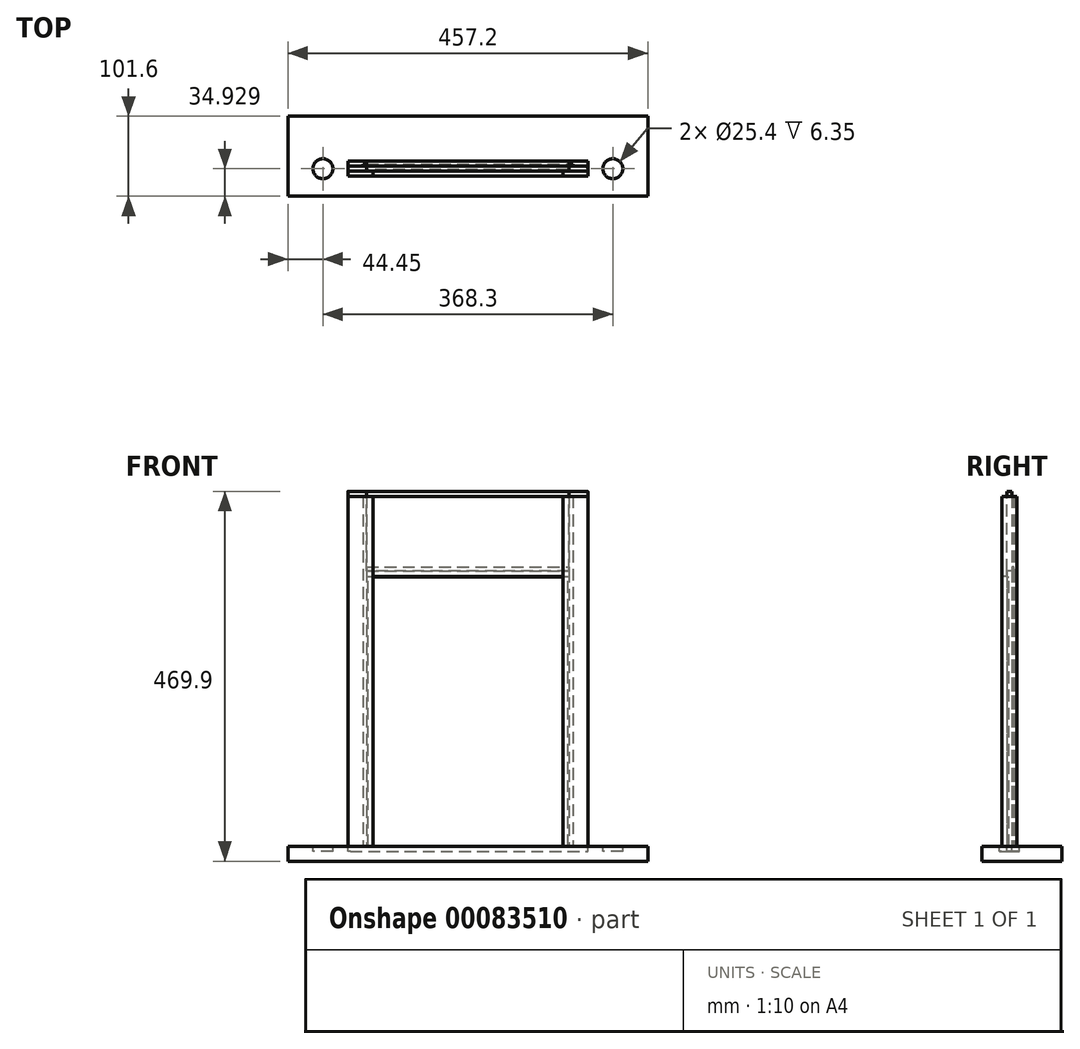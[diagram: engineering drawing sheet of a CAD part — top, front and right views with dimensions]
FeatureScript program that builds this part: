
annotation { "Feature Type Name" : "Feature", "Feature Type Description" : "" }
export const myFeature = defineFeature(function(context is Context, id is Id, definition is map)
    precondition{}
    {
        {
            var Q0;
            Q0=qCreatedBy(makeId("Front.planeOp"),FACE);
            var sketch = newSketch(context, id + "F0", { "sketchPlane" : qUnion([Q0])});
            skLineSegment(sketch, "E0.bottom", {"start": v(-127, -6.35) * mm, "end": v(127, -6.35) * mm});
            skLineSegment(sketch, "E0.top", {"start": v(-127, 349.25) * mm, "end": v(127, 349.25) * mm});
            skLineSegment(sketch, "E0.left", {"start": v(-127, -6.35) * mm, "end": v(-127, 349.25) * mm});
            skLineSegment(sketch, "E0.right", {"start": v(127, -6.35) * mm, "end": v(127, 349.25) * mm});
            skPoint(sketch, "E1", {"position": v(0, -6.35) * mm});
            skSolve(sketch);
        }
        {
            var Q0;
            Q0 = qSketchRegion(id + "F0", true);
            extrude(context, id + "F1", {"entities" : qUnion([Q0]), "depth" : 0.25 * mm});
        }
        {
            var Q0;
            Q0=qCreatedBy(makeId("Top.planeOp"),FACE);
            var sketch = newSketch(context, id + "F2", { "sketchPlane" : qUnion([Q0])});
            skLineSegment(sketch, "E2", {"start": v(-128.59, -2.29) * mm, "end": v(-120.65, -2.29) * mm});
            skLineSegment(sketch, "E3", {"start": v(-120.65, -2.29) * mm, "end": v(-120.65, -8.64) * mm});
            skLineSegment(sketch, "E4", {"start": v(-120.65, -8.64) * mm, "end": v(-152.4, -8.64) * mm});
            skLineSegment(sketch, "E5", {"start": v(-152.4, -8.64) * mm, "end": v(-152.4, 10.41) * mm});
            skLineSegment(sketch, "E6", {"start": v(-152.4, 10.41) * mm, "end": v(-128.59, 10.41) * mm});
            skLineSegment(sketch, "E7", {"start": v(-128.59, 4.06) * mm, "end": v(-128.59, -2.29) * mm});
            skLineSegment(sketch, "E8", {"start": v(-128.59, 4.06) * mm, "end": v(-133.35, 4.06) * mm});
            skLineSegment(sketch, "E9", {"start": v(-133.35, 4.06) * mm, "end": v(-133.35, 6.45) * mm});
            skLineSegment(sketch, "E10", {"start": v(-133.35, 6.45) * mm, "end": v(-128.59, 6.45) * mm});
            skLineSegment(sketch, "E11", {"start": v(-128.59, 6.45) * mm, "end": v(-128.59, 10.41) * mm});
            skSolve(sketch);
        }
        {
            var Q0;
            Q0 = qSketchRegion(id + "F2", true);
            extrude(context, id + "F3", {"entities" : qUnion([Q0]), "depth" : 444.5 * mm});
        }
        {
            var Q0;
            Q0=makeQuery(id+"F3.opExtrude","SWEPT_BODY",BODY,{"disambiguationData":[OSD([sQuery(id+"F2.wireOp",EDGE,"E2"),sQuery(id+"F2.wireOp",EDGE,"E3"),sQuery(id+"F2.wireOp",EDGE,"E4"),sQuery(id+"F2.wireOp",EDGE,"E5"),sQuery(id+"F2.wireOp",EDGE,"E6"),sQuery(id+"F2.wireOp",EDGE,"Aq9sfqS9-ccW6-2PHx-k0Lg-JicNwofaZmL2"),sQuery(id+"F2.wireOp",EDGE,"JhVU8ugL-pv20-RcfP-61ef-oaE8U2d1S3yL"),sQuery(id+"F2.wireOp",EDGE,"E7")])]});
            var Q1;
            Q1=qCreatedBy(makeId("Right.planeOp"),FACE);
            mirror(context, id + "F4", {"entities" : qUnion([Q0]), "mirrorPlane" : qUnion([Q1])});
        }
        {
            var Q0;
            Q0=makeQuery(id+"F3.opExtrude","CAP_FACE",FACE,{"disambiguationData":[OSD([sQuery(id+"F2.wireOp",EDGE,"E2"),sQuery(id+"F2.wireOp",EDGE,"E3"),sQuery(id+"F2.wireOp",EDGE,"E4"),sQuery(id+"F2.wireOp",EDGE,"E5"),sQuery(id+"F2.wireOp",EDGE,"E6"),sQuery(id+"F2.wireOp",EDGE,"E7"),sQuery(id+"F2.wireOp",EDGE,"E8"),sQuery(id+"F2.wireOp",EDGE,"E9"),sQuery(id+"F2.wireOp",EDGE,"E10"),sQuery(id+"F2.wireOp",EDGE,"E11")])],"isStart":false});
            var sketch = newSketch(context, id + "F5", { "sketchPlane" : qUnion([Q0])});
            skLineSegment(sketch, "E12.bottom", {"start": v(-128.59, 4.06) * mm, "end": v(-149.22, 4.06) * mm});
            skLineSegment(sketch, "E12.top", {"start": v(-128.59, -2.29) * mm, "end": v(-149.22, -2.29) * mm});
            skLineSegment(sketch, "E12.left", {"start": v(-128.59, 4.06) * mm, "end": v(-128.59, -2.29) * mm});
            skArc(sketch, "E13", {"start": v(-149.22, 4.06) * mm, "mid": v(-152.4, 0.89) * mm, "end": v(-149.22, -2.29) * mm});
            skSolve(sketch);
        }
        {
            var Q0;
            Q0 = qSketchRegion(id + "F5", true);
            extrude(context, id + "F6", {"entities" : qUnion([Q0]), "operationType" : NewBodyOperationType.ADD, "depth" : 6.35 * mm});
        }
        {
            var Q0;
            Q0=makeQuery(id+"F3.opExtrude","CAP_FACE",FACE,{"disambiguationData":[OSD([sQuery(id+"F2.wireOp",EDGE,"E2"),sQuery(id+"F2.wireOp",EDGE,"E3"),sQuery(id+"F2.wireOp",EDGE,"E4"),sQuery(id+"F2.wireOp",EDGE,"E5"),sQuery(id+"F2.wireOp",EDGE,"E6"),sQuery(id+"F2.wireOp",EDGE,"E7"),sQuery(id+"F2.wireOp",EDGE,"E8"),sQuery(id+"F2.wireOp",EDGE,"E9"),sQuery(id+"F2.wireOp",EDGE,"E10"),sQuery(id+"F2.wireOp",EDGE,"E11")])],"isStart":true});
            var sketch = newSketch(context, id + "F7", { "sketchPlane" : qUnion([Q0])});
            skLineSegment(sketch, "E14.0", {"start": v(-128.59, 2.29) * mm, "end": v(-149.22, 2.29) * mm});
            skArc(sketch, "E15.0", {"start": v(-149.22, -4.06) * mm, "mid": v(-152.4, -0.89) * mm, "end": v(-149.22, 2.29) * mm});
            skLineSegment(sketch, "E16.0", {"start": v(-128.59, -4.06) * mm, "end": v(-149.22, -4.06) * mm});
            skLineSegment(sketch, "E17.0", {"start": v(-128.59, -4.06) * mm, "end": v(-128.59, 2.29) * mm});
            skSolve(sketch);
        }
        {
            var Q0;
            Q0 = qSketchRegion(id + "F7", true);
            extrude(context, id + "F8", {"entities" : qUnion([Q0]), "operationType" : NewBodyOperationType.ADD, "depth" : 6.35 * mm});
        }
        {
            var Q0;
            Q0=makeQuery(id+"F4.opPattern","COPY",BODY,{"derivedFrom":makeQuery(id+"F3.opExtrude","SWEPT_BODY",BODY,{"disambiguationData":[OSD([sQuery(id+"F2.wireOp",EDGE,"E2"),sQuery(id+"F2.wireOp",EDGE,"E3"),sQuery(id+"F2.wireOp",EDGE,"E4"),sQuery(id+"F2.wireOp",EDGE,"E5"),sQuery(id+"F2.wireOp",EDGE,"E6"),sQuery(id+"F2.wireOp",EDGE,"E7"),sQuery(id+"F2.wireOp",EDGE,"E8"),sQuery(id+"F2.wireOp",EDGE,"E9"),sQuery(id+"F2.wireOp",EDGE,"E10"),sQuery(id+"F2.wireOp",EDGE,"E11")])]}),"instanceName":"1"});
            deleteBodies(context, id + "F9", {"entities" : qUnion([Q0])});
        }
        {
            var Q0;
            {var subQ0=sQuery(id+"F2.wireOp",EDGE,"E4");var subQ1=sQuery(id+"F2.wireOp",EDGE,"E3");var subQ2=sQuery(id+"F2.wireOp",EDGE,"E7");var subQ3=sQuery(id+"F2.wireOp",EDGE,"E5");var subQ4=sQuery(id+"F2.wireOp",EDGE,"E2");var subQ5=makeQuery(id+"F3.opExtrude","CAP_FACE",FACE,{"disambiguationData":[OSD([subQ4,subQ1,subQ0,subQ3,sQuery(id+"F2.wireOp",EDGE,"E6"),subQ2,sQuery(id+"F2.wireOp",EDGE,"E8"),sQuery(id+"F2.wireOp",EDGE,"E9"),sQuery(id+"F2.wireOp",EDGE,"E10"),sQuery(id+"F2.wireOp",EDGE,"E11")])],"isStart":false});Q0=makeQuery(id+"F6.boolean.opBoolean","SPLIT",FACE,{"disambiguationData":[TD([makeQuery(id+"F3.opExtrude","SWEPT_FACE",FACE,{"disambiguationData":[OSD([subQ4])]})])],"derivedFrom":subQ5});}
            var sketch = newSketch(context, id + "F10", { "sketchPlane" : qUnion([Q0])});
            skLineSegment(sketch, "E18.0", {"start": v(-128.59, -2.29) * mm, "end": v(-120.65, -2.29) * mm});
            skLineSegment(sketch, "E19.0", {"start": v(-120.65, -2.29) * mm, "end": v(-120.65, -8.64) * mm});
            skLineSegment(sketch, "E20", {"start": v(-128.59, -2.29) * mm, "end": v(-128.59, 10.41) * mm});
            skLineSegment(sketch, "E21", {"start": v(-128.59, 10.41) * mm, "end": v(0, 10.41) * mm});
            skLineSegment(sketch, "E22", {"start": v(-120.65, -8.64) * mm, "end": v(0, -8.64) * mm});
            skLineSegment(sketch, "E23", {"start": v(0, 16.31) * mm, "end": v(0, -13.97) * mm, "construction": true});
            skLineSegment(sketch, "E24.MirrorCS", {"start": v(128.59, 10.41) * mm, "end": v(0, 10.41) * mm});
            skLineSegment(sketch, "E25.MirrorCS", {"start": v(120.65, -8.64) * mm, "end": v(0, -8.64) * mm});
            skLineSegment(sketch, "E26.MirrorCS", {"start": v(128.59, -2.29) * mm, "end": v(128.59, 10.41) * mm});
            skLineSegment(sketch, "E27.MirrorCS", {"start": v(128.59, -2.29) * mm, "end": v(120.65, -2.29) * mm});
            skLineSegment(sketch, "E28.MirrorCS", {"start": v(120.65, -2.29) * mm, "end": v(120.65, -8.64) * mm});
            skSolve(sketch);
        }
        {
            var Q0;
            Q0 = qSketchRegion(id + "F10", true);
            extrude(context, id + "F11", {"entities" : qUnion([Q0]), "oppositeDirection" : true, "depth" : 101.6 * mm});
        }
        {
            var Q0;
            Q0=qCreatedBy(makeId("Right.planeOp"),FACE);
            var sketch = newSketch(context, id + "F12", { "sketchPlane" : qUnion([Q0])});
            skLineSegment(sketch, "E29", {"start": v(-2.29, 342.1) * mm, "end": v(-2.29, 350.04) * mm});
            skLineSegment(sketch, "E30", {"start": v(-2.29, 350.04) * mm, "end": v(4.06, 350.04) * mm});
            skLineSegment(sketch, "E31", {"start": v(4.06, 350.04) * mm, "end": v(4.06, 354.8) * mm});
            skLineSegment(sketch, "E32", {"start": v(4.06, 354.8) * mm, "end": v(6.45, 354.8) * mm});
            skLineSegment(sketch, "E33", {"start": v(6.45, 354.8) * mm, "end": v(6.45, 350.04) * mm});
            skLineSegment(sketch, "E34", {"start": v(11.2, 342.1) * mm, "end": v(-2.29, 342.1) * mm});
            skLineSegment(sketch, "E35", {"start": v(6.45, 350.04) * mm, "end": v(11.2, 350.04) * mm});
            skLineSegment(sketch, "E36", {"start": v(11.2, 350.04) * mm, "end": v(11.2, 342.1) * mm});
            skSolve(sketch);
        }
        {
            var Q0;
            Q0 = qSketchRegion(id + "F12", true);
            var Q1;
            Q1=makeQuery(id+"F11.opExtrude","SWEPT_FACE",FACE,{"disambiguationData":[OSD([sQuery(id+"F10.wireOp",EDGE,"E20")])]});
            var Q2;
            Q2=makeQuery(id+"F11.opExtrude","SWEPT_FACE",FACE,{"disambiguationData":[OSD([sQuery(id+"F10.wireOp",EDGE,"E26.MirrorCS")])]});
            extrude(context, id + "F13", {"entities" : qUnion([Q0]), "operationType" : NewBodyOperationType.REMOVE, "endBound" : BoundingType.UP_TO_SURFACE, "oppositeDirection" : true, "endBoundEntityFace" : qUnion([Q1]), "depth" : 25.4 * mm, "hasSecondDirection" : true, "secondDirectionBound" : SecondDirectionBoundingType.UP_TO_SURFACE, "secondDirectionOppositeDirection" : false, "secondDirectionBoundEntityFace" : qUnion([Q2]), "secondDirectionDepth" : 25.4 * mm});
        }
        {
            var Q0;
            Q0=makeQuery(id+"F11.opExtrude","CAP_FACE",FACE,{"disambiguationData":[OSD([sQuery(id+"F10.wireOp",EDGE,"E18.0"),sQuery(id+"F10.wireOp",EDGE,"E19.0"),sQuery(id+"F10.wireOp",EDGE,"E20"),sQuery(id+"F10.wireOp",EDGE,"E21"),sQuery(id+"F10.wireOp",EDGE,"E22"),sQuery(id+"F10.wireOp",EDGE,"E24.MirrorCS"),sQuery(id+"F10.wireOp",EDGE,"E25.MirrorCS"),sQuery(id+"F10.wireOp",EDGE,"E26.MirrorCS"),sQuery(id+"F10.wireOp",EDGE,"E27.MirrorCS"),sQuery(id+"F10.wireOp",EDGE,"E28.MirrorCS")])],"isStart":true});
            var sketch = newSketch(context, id + "F14", { "sketchPlane" : qUnion([Q0])});
            skLineSegment(sketch, "E37.bottom", {"start": v(-128.59, 4.06) * mm, "end": v(128.59, 4.06) * mm});
            skLineSegment(sketch, "E37.top", {"start": v(-128.59, -2.29) * mm, "end": v(128.59, -2.29) * mm});
            skLineSegment(sketch, "E37.left", {"start": v(-128.59, 4.06) * mm, "end": v(-128.59, -2.29) * mm});
            skLineSegment(sketch, "E37.right", {"start": v(128.59, 4.06) * mm, "end": v(128.59, -2.29) * mm});
            skSolve(sketch);
        }
        {
            var Q0;
            Q0 = qSketchRegion(id + "F14", true);
            extrude(context, id + "F15", {"entities" : qUnion([Q0]), "operationType" : NewBodyOperationType.ADD, "depth" : 6.35 * mm});
        }
        {
            var Q0;
            Q0=makeQuery(id+"F3.opExtrude","SWEPT_BODY",BODY,{"disambiguationData":[OSD([sQuery(id+"F2.wireOp",EDGE,"E2"),sQuery(id+"F2.wireOp",EDGE,"E3"),sQuery(id+"F2.wireOp",EDGE,"E4"),sQuery(id+"F2.wireOp",EDGE,"E5"),sQuery(id+"F2.wireOp",EDGE,"E6"),sQuery(id+"F2.wireOp",EDGE,"E7"),sQuery(id+"F2.wireOp",EDGE,"E8"),sQuery(id+"F2.wireOp",EDGE,"E9"),sQuery(id+"F2.wireOp",EDGE,"E10"),sQuery(id+"F2.wireOp",EDGE,"E11")])]});
            var Q1;
            Q1=qCreatedBy(makeId("Right.planeOp"),FACE);
            mirror(context, id + "F16", {"entities" : qUnion([Q0]), "mirrorPlane" : qUnion([Q1])});
        }
        {
            var Q0;
            Q0=qCreatedBy(makeId("Top.planeOp"),FACE);
            var sketch = newSketch(context, id + "F17", { "sketchPlane" : qUnion([Q0])});
            skLineSegment(sketch, "E38.bottom", {"start": v(-228.6, 67.56) * mm, "end": v(228.6, 67.56) * mm});
            skLineSegment(sketch, "E38.top", {"start": v(-228.6, -34.04) * mm, "end": v(228.6, -34.04) * mm});
            skLineSegment(sketch, "E38.left", {"start": v(-228.6, 67.56) * mm, "end": v(-228.6, -34.04) * mm});
            skLineSegment(sketch, "E38.right", {"start": v(228.6, 67.56) * mm, "end": v(228.6, -34.04) * mm});
            skSolve(sketch);
        }
        {
            var Q0;
            Q0 = qSketchRegion(id + "F17", true);
            extrude(context, id + "F18", {"entities" : qUnion([Q0]), "oppositeDirection" : true, "depth" : 19.05 * mm});
        }
        {
            var Q0;
            Q0=makeQuery(id+"F18.opExtrude","CAP_FACE",FACE,{"disambiguationData":[OSD([sQuery(id+"F17.wireOp",EDGE,"E38.bottom"),sQuery(id+"F17.wireOp",EDGE,"E38.top"),sQuery(id+"F17.wireOp",EDGE,"E38.left"),sQuery(id+"F17.wireOp",EDGE,"E38.right")])],"isStart":true});
            var sketch = newSketch(context, id + "F19", { "sketchPlane" : qUnion([Q0])});
            skCircle(sketch, "E39", {"center": v(-184.15, 0.89) * mm, "radius": 12.7 * mm});
            skLineSegment(sketch, "E40", {"start": v(-184.15, 0.89) * mm, "end": v(184.15, 0.89) * mm, "construction": true});
            skCircle(sketch, "E41", {"center": v(184.15, 0.89) * mm, "radius": 12.7 * mm});
            skSolve(sketch);
        }
        {
            var Q0;
            Q0 = qSketchRegion(id + "F19", true);
            extrude(context, id + "F20", {"entities" : qUnion([Q0]), "operationType" : NewBodyOperationType.REMOVE, "oppositeDirection" : true, "depth" : 6.35 * mm});
        }
        {
            var Q0;
            Q0=makeQuery(id+"F18.opExtrude","CAP_FACE",FACE,{"disambiguationData":[OSD([sQuery(id+"F17.wireOp",EDGE,"E38.bottom"),sQuery(id+"F17.wireOp",EDGE,"E38.top"),sQuery(id+"F17.wireOp",EDGE,"E38.left"),sQuery(id+"F17.wireOp",EDGE,"E38.right")])],"isStart":true});
            var sketch = newSketch(context, id + "F21", { "sketchPlane" : qUnion([Q0])});
            skArc(sketch, "E42.0", {"start": v(-149.22, 4.06) * mm, "mid": v(-152.4, 0.89) * mm, "end": v(-149.22, -2.29) * mm});
            skLineSegment(sketch, "E43", {"start": v(-149.22, 4.06) * mm, "end": v(0, 4.06) * mm});
            skLineSegment(sketch, "E44", {"start": v(-149.22, -2.29) * mm, "end": v(0, -2.29) * mm});
            skLineSegment(sketch, "E45", {"start": v(0, 9) * mm, "end": v(0, -8.06) * mm, "construction": true});
            skArc(sketch, "E46.MirrorCS", {"start": v(149.22, 4.06) * mm, "mid": v(152.4, 0.89) * mm, "end": v(149.22, -2.29) * mm});
            skLineSegment(sketch, "E47.MirrorCS", {"start": v(149.22, -2.29) * mm, "end": v(0, -2.29) * mm});
            skLineSegment(sketch, "E48.MirrorCS", {"start": v(149.22, 4.06) * mm, "end": v(0, 4.06) * mm});
            skSolve(sketch);
        }
        {
            var Q0;
            Q0 = qSketchRegion(id + "F21", true);
            extrude(context, id + "F22", {"entities" : qUnion([Q0]), "operationType" : NewBodyOperationType.REMOVE, "oppositeDirection" : true, "depth" : 6.35 * mm});
        }
    });
